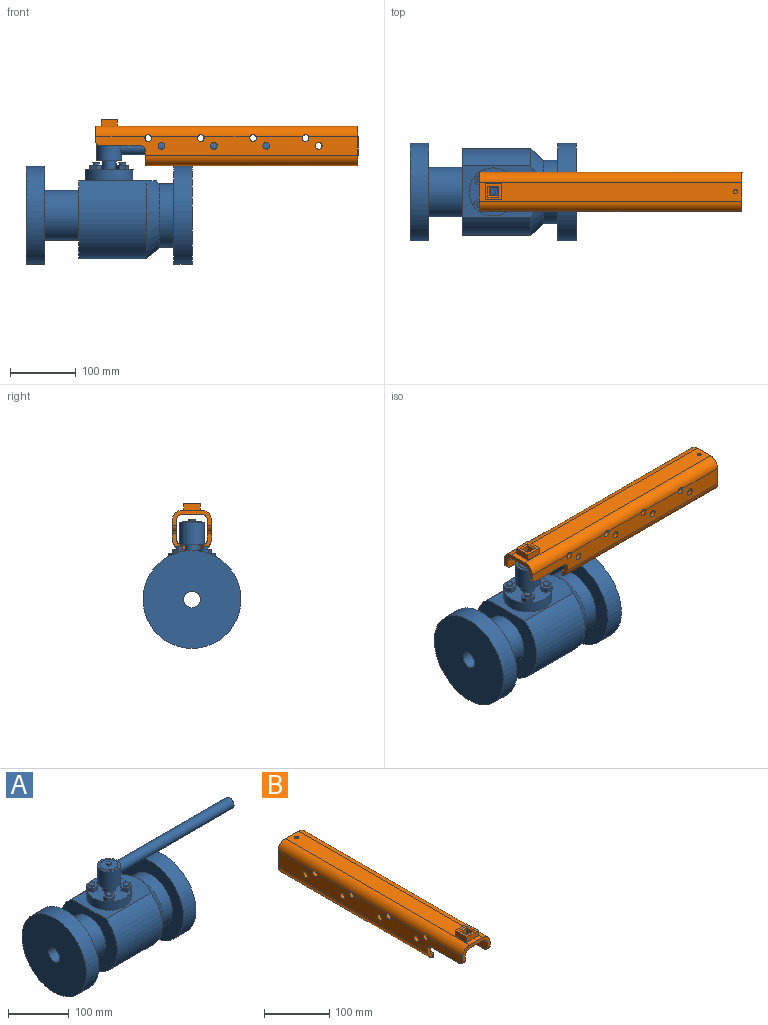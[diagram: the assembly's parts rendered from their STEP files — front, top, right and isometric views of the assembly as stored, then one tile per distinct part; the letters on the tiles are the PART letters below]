
ASSEMBLY  parts=2 mates=1
PART A: 70 faces, bbox 407x149.5x196.9 mm
  f0: plane 29.5x29.5mm, normal (0,0,1), area 628.1mm2, adj f61,f62,f63,f64,f65,f66,f67
  f1: cylinder r=19.09mm len=38.18mm, axis (0,0,1), area 3788.9mm2, adj f57,f58,f59
  f2: cylinder r=10.64mm len=21.27mm, axis (0,0,-1), area 900.7mm2, adj f3,f57
  f3: plane 73.25x73.25mm, normal (0,0,1), area 2868mm2, adj f2,f16,f17,f18,f19,f20,f21,f22
  f4: plane 149.5x149.5mm, normal (-1,0,0), area 17047.1mm2, adj f5,f69
  f5: cylinder r=74.75mm len=149.5mm, axis (-1,0,0), area 13420.8mm2, adj f4,f6
  f6: plane 149.5x149.5mm, normal (1,0,0), area 12995.9mm2, adj f5,f7
  f7: cylinder r=38.09mm len=76.18mm, axis (-1,0,0), area 12445mm2, adj f6,f8
  f8: plane 131.85x118.6mm, normal (-1,0,0), area 8379.6mm2, adj f7,f9,f15
  f9: cylinder r=65.92mm len=131.85mm, axis (-1,0,0), area 34230.6mm2, adj f8,f10,f15
  f10: cone r=65.92mm half-angle=42.9deg, axis (-1,0,0), area 8116.7mm2, adj f9,f11,f15
  f11: cylinder r=48.56mm len=97.13mm, axis (-1,0,0), area 6769.8mm2, adj f10,f12
  f12: plane 149.5x149.5mm, normal (-1,0,0), area 10144.3mm2, adj f11,f13
  f13: cylinder r=74.75mm len=149.5mm, axis (-1,0,0), area 13420.8mm2, adj f12,f14
  f14: plane 149.5x149.5mm, normal (1,0,0), area 17047.1mm2, adj f13,f69
  f15: plane 118.25x79.31mm, normal (0,0,1), area 4768.9mm2, adj f8,f9,f10,f16
  f16: cylinder r=36.62mm len=73.25mm, axis (0,0,-1), area 3930.9mm2, adj f3,f15,f24,f27,f37,f47
  f17: plane 8.5x7.18mm, normal (0.87,0.5,0), area 70.4mm2, adj f3,f18,f22,f23
  f18: plane 9.85x7.18mm, normal (0,1,0), area 70.7mm2, adj f3,f17,f19,f23,f24
  f19: plane 8.5x7.18mm, normal (-0.87,0.5,0), area 70.4mm2, adj f3,f18,f20,f23,f24
  f20: plane 8.5x7.18mm, normal (-0.87,-0.5,0), area 70.4mm2, adj f3,f19,f21,f23
  f21: plane 9.85x7.18mm, normal (0,-1,0), area 70.7mm2, adj f3,f20,f22,f23
  f22: plane 8.5x7.18mm, normal (0.87,-0.5,0), area 70.4mm2, adj f3,f17,f21,f23
  f23: plane 19.6x17mm, normal (0,0,1), area 171.7mm2, adj f17,f18,f19,f20,f21,f22,f26
  f24: plane 3.66x3.42mm, normal (0,0,-1), area 2.6mm2, adj f16,f18,f19
  f25: plane 10x10mm, normal (0,0,1), area 78.5mm2, adj f26
  f26: cylinder r=5mm len=10mm, axis (0,0,-1), area 100.3mm2, adj f23,f25
  f27: plane 3.66x3.42mm, normal (0,0,-1), area 2.6mm2, adj f16,f28,f29
  f28: plane 9.85x7.18mm, normal (-1,0,0), area 70.7mm2, adj f3,f27,f29,f33,f34
  f29: plane 8.5x7.18mm, normal (-0.5,-0.87,0), area 70.4mm2, adj f3,f27,f28,f30,f34
  f30: plane 8.5x7.18mm, normal (0.5,-0.87,0), area 70.4mm2, adj f3,f29,f31,f34
  f31: plane 9.85x7.18mm, normal (1,0,0), area 70.7mm2, adj f3,f30,f32,f34
  f32: plane 8.5x7.18mm, normal (0.5,0.87,0), area 70.4mm2, adj f3,f31,f33,f34
  f33: plane 8.5x7.18mm, normal (-0.5,0.87,0), area 70.4mm2, adj f3,f28,f32,f34
  f34: plane 19.6x17mm, normal (0,0,1), area 171.7mm2, adj f28,f29,f30,f31,f32,f33,f36
  f35: plane 10x10mm, normal (0,0,1), area 78.5mm2, adj f36
  f36: cylinder r=5mm len=10mm, axis (0,0,-1), area 100.3mm2, adj f34,f35
  f37: plane 3.66x3.42mm, normal (0,0,-1), area 2.6mm2, adj f16,f38,f39
  f38: plane 9.85x7.18mm, normal (0,-1,0), area 70.7mm2, adj f3,f37,f39,f43,f44
  f39: plane 8.5x7.18mm, normal (0.87,-0.5,0), area 70.4mm2, adj f3,f37,f38,f40,f44
  f40: plane 8.5x7.18mm, normal (0.87,0.5,0), area 70.4mm2, adj f3,f39,f41,f44
  f41: plane 9.85x7.18mm, normal (0,1,0), area 70.7mm2, adj f3,f40,f42,f44
  f42: plane 8.5x7.18mm, normal (-0.87,0.5,0), area 70.4mm2, adj f3,f41,f43,f44
  f43: plane 8.5x7.18mm, normal (-0.87,-0.5,0), area 70.4mm2, adj f3,f38,f42,f44
  f44: plane 19.6x17mm, normal (0,0,1), area 171.7mm2, adj f38,f39,f40,f41,f42,f43,f46
  f45: plane 10x10mm, normal (0,0,1), area 78.5mm2, adj f46
  f46: cylinder r=5mm len=10mm, axis (0,0,-1), area 100.3mm2, adj f44,f45
  f47: plane 3.66x3.42mm, normal (0,0,-1), area 2.6mm2, adj f16,f48,f49
  f48: plane 9.85x7.18mm, normal (1,0,0), area 70.7mm2, adj f3,f47,f49,f53,f54
  f49: plane 8.5x7.18mm, normal (0.5,0.87,0), area 70.4mm2, adj f3,f47,f48,f50,f54
  f50: plane 8.5x7.18mm, normal (-0.5,0.87,0), area 70.4mm2, adj f3,f49,f51,f54
  f51: plane 9.85x7.18mm, normal (-1,0,0), area 70.7mm2, adj f3,f50,f52,f54
  f52: plane 8.5x7.18mm, normal (-0.5,-0.87,0), area 70.4mm2, adj f3,f51,f53,f54
  f53: plane 8.5x7.18mm, normal (0.5,-0.87,0), area 70.4mm2, adj f3,f48,f52,f54
  f54: plane 19.6x17mm, normal (0,0,1), area 171.7mm2, adj f48,f49,f50,f51,f52,f53,f56
  f55: plane 10x10mm, normal (0,0,1), area 78.5mm2, adj f56
  f56: cylinder r=5mm len=10mm, axis (0,0,-1), area 100.3mm2, adj f54,f55
  f57: plane 38.18x38.18mm, normal (0,0,-1), area 789.4mm2, adj f1,f2
  f58: plane 38.18x38.18mm, normal (0,0,1), area 461.3mm2, adj f1,f61
  f59: cylinder r=9.95mm len=263.71mm, axis (-1,0,0), area 16392.9mm2, adj f1,f60
  f60: plane 19.89x19.89mm, normal (1,0,0), area 310.9mm2, adj f59
  f61: cylinder r=14.75mm len=29.5mm, axis (0,0,-1), area 92.7mm2, adj f0,f58
  f62: plane 4x3.65mm, normal (0.49,0.87,0), area 16.8mm2, adj f0,f63,f67,f68
  f63: plane 4x3.65mm, normal (-0.49,0.87,0), area 16.8mm2, adj f0,f62,f64,f68
  f64: plane 4.66x3.65mm, normal (-1,0,0), area 17mm2, adj f0,f63,f65,f68
  f65: plane 4x3.65mm, normal (-0.49,-0.87,0), area 16.8mm2, adj f0,f64,f66,f68
  f66: plane 4x3.65mm, normal (0.49,-0.87,0), area 16.8mm2, adj f0,f65,f67,f68
  f67: plane 4.66x3.65mm, normal (1,0,0), area 17mm2, adj f0,f62,f66,f68
  f68: plane 9.2x8mm, normal (0,0,1), area 55.4mm2, adj f62,f63,f64,f65,f66,f67
  f69: cylinder r=12.7mm len=254mm, axis (1,0,0), area 20268.3mm2, adj f4,f14
PART B: 63 faces, bbox 60x400x70 mm
  f0: plane 281x28.5mm, normal (0,0,-1), area 7853mm2, adj f10,f17,f18,f47,f50,f51
  f1: plane 281x28.5mm, normal (0,0,1), area 7853mm2, adj f13,f14,f18,f47,f50,f51
  f2: plane 22.81x9.75mm, normal (0,-1,0), area 137.2mm2, adj f9,f10,f14,f15,f52,f54
  f3: plane 400x28.5mm, normal (0,0,-1), area 11210.4mm2, adj f4,f11,f16,f18,f41,f42,f43,f44
  f4: plane 60x24mm, normal (0,-1,0), area 534.3mm2, adj f3,f5,f6,f7,f8,f9,f11,f12
  f5: plane 400x28.5mm, normal (1,0,0), area 9752.2mm2, adj f4,f6,f17,f18,f19,f21,f30,f31
  f6: cylinder r=15.75mm len=400mm, axis (0,1,0), area 9821mm2, adj f4,f5,f7,f18,f31,f32,f33,f37
  f7: plane 400x28.5mm, normal (0,0,1), area 10746.7mm2, adj f4,f6,f8,f18,f38,f39,f40,f45
  f8: cylinder r=15.75mm len=400mm, axis (0,1,0), area 9821mm2, adj f4,f7,f9,f18,f22,f23,f24,f25
  f9: plane 400x28.5mm, normal (-1,0,0), area 9752.2mm2, adj f2,f4,f8,f10,f18,f20,f22,f23
  f10: cylinder r=15.75mm len=325mm, axis (0,1,0), area 8032.7mm2, adj f0,f2,f9,f18,f48,f52
  f11: cylinder r=9.45mm len=400mm, axis (0,1,0), area 5861mm2, adj f3,f4,f12,f18,f31,f32,f33,f37
  f12: plane 400x28.44mm, normal (-1,0,0), area 9731.6mm2, adj f4,f11,f13,f18,f19,f21,f30,f31
  f13: cylinder r=9.45mm len=325mm, axis (0,1,0), area 4816.4mm2, adj f1,f12,f18,f19,f49,f53
  f14: cylinder r=9.45mm len=325mm, axis (0,1,0), area 4816.4mm2, adj f1,f2,f15,f18,f48,f52
  f15: plane 400x28.44mm, normal (1,0,0), area 9731.6mm2, adj f2,f4,f14,f16,f18,f20,f22,f23
  f16: cylinder r=9.45mm len=400mm, axis (0,1,0), area 5860.9mm2, adj f3,f4,f15,f18,f22,f23,f24,f25
  f17: cylinder r=15.75mm len=325mm, axis (0,1,0), area 8032.7mm2, adj f0,f5,f18,f19,f49,f53
  f18: plane 60x60mm, normal (0,1,0), area 1219.8mm2, adj f0,f1,f3,f5,f6,f7,f8,f9
  f19: plane 22.81x9.75mm, normal (0,-1,0), area 137.2mm2, adj f5,f12,f13,f17,f53,f57
  f20: plane 63x6.3mm, normal (0,0,-1), area 396.9mm2, adj f9,f15,f54,f55
  f21: plane 63x6.3mm, normal (0,0,-1), area 396.9mm2, adj f5,f12,f56,f57
  f22: cylinder r=5.1mm len=10.2mm, axis (1,0,0), area 203mm2, adj f8,f9,f15,f16
  f23: cylinder r=5.1mm len=10.2mm, axis (1,0,0), area 203mm2, adj f8,f9,f15,f16
  f24: cylinder r=5.1mm len=10.2mm, axis (1,0,0), area 203mm2, adj f8,f9,f15,f16
  f25: cylinder r=5.1mm len=10.2mm, axis (1,0,0), area 203mm2, adj f8,f9,f15,f16
  f26: cylinder r=5.1mm len=10.2mm, axis (1,0,0), area 201.9mm2, adj f9,f15
  f27: cylinder r=5.1mm len=10.2mm, axis (1,0,0), area 201.9mm2, adj f9,f15
  f28: cylinder r=5.1mm len=10.2mm, axis (1,0,0), area 201.9mm2, adj f9,f15
  f29: cylinder r=5.1mm len=10.2mm, axis (1,0,0), area 201.9mm2, adj f9,f15
  f30: cylinder r=5.1mm len=10.2mm, axis (1,0,0), area 201.9mm2, adj f5,f12
  f31: cylinder r=5.1mm len=10.2mm, axis (1,0,0), area 203mm2, adj f5,f6,f11,f12
  f32: cylinder r=5.1mm len=10.2mm, axis (1,0,0), area 203mm2, adj f5,f6,f11,f12
  f33: cylinder r=5.1mm len=10.2mm, axis (1,0,0), area 203mm2, adj f5,f6,f11,f12
  f34: cylinder r=5.1mm len=10.2mm, axis (1,0,0), area 201.9mm2, adj f5,f12
  f35: cylinder r=5.1mm len=10.2mm, axis (1,0,0), area 201.9mm2, adj f5,f12
  f36: cylinder r=5.1mm len=10.2mm, axis (1,0,0), area 201.9mm2, adj f5,f12
  f37: cylinder r=5.1mm len=10.2mm, axis (1,0,0), area 203mm2, adj f5,f6,f11,f12
  f38: plane 25x10mm, normal (0,-1,0), area 250mm2, adj f7,f39,f45,f46
  f39: plane 25x10mm, normal (1,0,0), area 250mm2, adj f7,f38,f40,f46
  f40: plane 25x10mm, normal (0,1,0), area 250mm2, adj f7,f39,f45,f46
  f41: plane 14.33x12.7mm, normal (-1,0,0), area 182mm2, adj f3,f42,f44,f58
  f42: plane 14.33x12.7mm, normal (0,1,0), area 182mm2, adj f3,f41,f43,f59
  f43: plane 14.33x12.7mm, normal (1,0,0), area 182mm2, adj f3,f42,f44,f61
  f44: plane 14.33x12.7mm, normal (0,-1,0), area 182mm2, adj f3,f41,f43,f60
  f45: plane 25x10mm, normal (-1,0,0), area 250mm2, adj f7,f38,f40,f46
  f46: plane 25x25mm, normal (0,0,1), area 346.1mm2, adj f38,f39,f40,f45,f58,f59,f60,f61
  f47: plane 16.5x6.33mm, normal (0,-1,0), area 104.4mm2, adj f0,f1,f50,f51
  f48: plane 38x6.33mm, normal (1,0,0), area 240.5mm2, adj f10,f14,f50,f52
  f49: plane 38x6.33mm, normal (-1,0,0), area 240.5mm2, adj f13,f17,f51,f53
  f50: cylinder r=6mm len=6.33mm, axis (0,0,1), area 59.7mm2, adj f0,f1,f47,f48
  f51: cylinder r=6mm len=6.33mm, axis (0,0,-1), area 59.7mm2, adj f0,f1,f47,f49
  f52: cylinder r=6mm len=8.48mm, axis (0,0,-1), area 61.5mm2, adj f2,f10,f14,f48
  f53: cylinder r=6mm len=8.48mm, axis (0,0,1), area 61.5mm2, adj f13,f17,f19,f49
  f54: cylinder r=6mm len=6.3mm, axis (-1,0,0), area 59.4mm2, adj f2,f9,f15,f20
  f55: cylinder r=6mm len=6.3mm, axis (1,0,0), area 59.4mm2, adj f4,f9,f15,f20
  f56: cylinder r=6mm len=6.3mm, axis (1,0,0), area 59.4mm2, adj f4,f5,f12,f21
  f57: cylinder r=6mm len=6.3mm, axis (-1,0,0), area 59.4mm2, adj f5,f12,f19,f21
  f58: plane 16.7x2mm, normal (-0.71,0,0.71), area 41.6mm2, adj f41,f46,f59,f60
  f59: plane 16.7x2mm, normal (0,0.71,0.71), area 41.6mm2, adj f42,f46,f58,f61
  f60: plane 16.7x2mm, normal (0,-0.71,0.71), area 41.6mm2, adj f44,f46,f58,f61
  f61: plane 16.7x2mm, normal (0.71,0,0.71), area 41.6mm2, adj f43,f46,f59,f60
  f62: cylinder r=3mm len=6.33mm, axis (0,0,1), area 119.3mm2, adj f3,f7
PLACE A at identity fixed
PLACE B rot(axis=(0,0,-1),90deg) t=(379.61,0.06,106.1)mm
MATE parallel B.f3 <-> A.f61  axis (0,0,-1) through (181.71,0.06,129.77)mm
